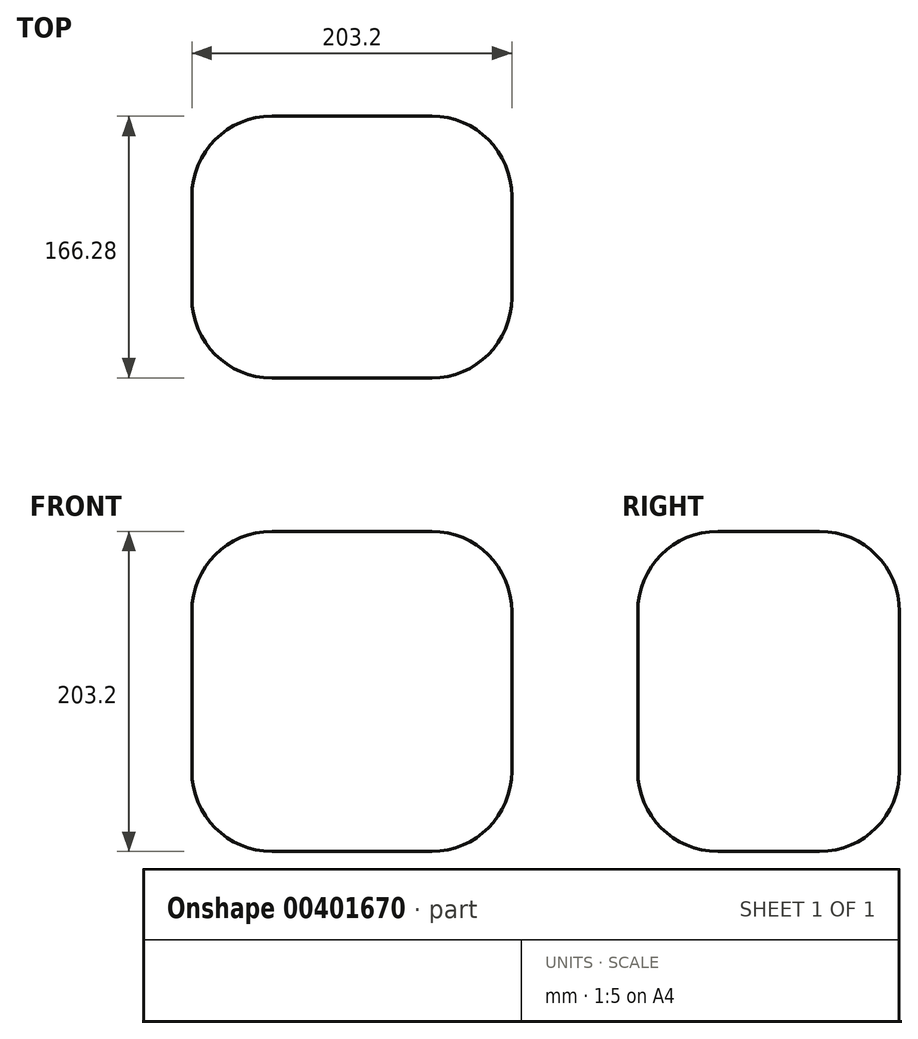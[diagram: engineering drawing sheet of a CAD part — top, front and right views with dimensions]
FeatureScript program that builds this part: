
annotation { "Feature Type Name" : "Feature", "Feature Type Description" : "" }
export const myFeature = defineFeature(function(context is Context, id is Id, definition is map)
    precondition{}
    {
        {
            var Q0;
            Q0=qCreatedBy(makeId("Front.planeOp"),FACE);
            var sketch = newSketch(context, id + "F0", { "sketchPlane" : qUnion([Q0])});
            skLineSegment(sketch, "E0.bottom", {"start": v(-100.4, 111.28) * mm, "end": v(102.8, 111.28) * mm});
            skLineSegment(sketch, "E0.top", {"start": v(-100.4, -91.92) * mm, "end": v(102.8, -91.92) * mm});
            skLineSegment(sketch, "E0.left", {"start": v(-100.4, 111.28) * mm, "end": v(-100.4, -91.92) * mm});
            skLineSegment(sketch, "E0.right", {"start": v(102.8, 111.28) * mm, "end": v(102.8, -91.92) * mm});
            skSolve(sketch);
        }
        {
            var Q0;
            Q0 = qSketchRegion(id + "F0", true);
            extrude(context, id + "F1", {"entities" : qUnion([Q0]), "depth" : 166.28 * mm});
        }
        {
            var Q0;
            Q0=makeQuery(id+"F1.opExtrude","SWEPT_EDGE",EDGE,{"disambiguationData":[OSD([sQuery(id+"F0.wireOp",EDGE,"E0.bottom"),sQuery(id+"F0.wireOp",EDGE,"E0.right")])]});
            var Q1;
            Q1=makeQuery(id+"F1.opExtrude","CAP_EDGE",EDGE,{"disambiguationData":[OSD([sQuery(id+"F0.wireOp",EDGE,"E0.bottom")])],"isStart":false});
            var Q2;
            Q2=makeQuery(id+"F1.opExtrude","CAP_EDGE",EDGE,{"disambiguationData":[OSD([sQuery(id+"F0.wireOp",EDGE,"E0.right")])],"isStart":false});
            var Q3;
            Q3=makeQuery(id+"F1.opExtrude","CAP_EDGE",EDGE,{"disambiguationData":[OSD([sQuery(id+"F0.wireOp",EDGE,"E0.bottom")])],"isStart":true});
            var Q4;
            Q4=makeQuery(id+"F1.opExtrude","SWEPT_EDGE",EDGE,{"disambiguationData":[OSD([sQuery(id+"F0.wireOp",EDGE,"E0.bottom"),sQuery(id+"F0.wireOp",EDGE,"E0.left")])]});
            var Q5;
            Q5=makeQuery(id+"F1.opExtrude","CAP_EDGE",EDGE,{"disambiguationData":[OSD([sQuery(id+"F0.wireOp",EDGE,"E0.left")])],"isStart":false});
            var Q6;
            Q6=makeQuery(id+"F1.opExtrude","CAP_EDGE",EDGE,{"disambiguationData":[OSD([sQuery(id+"F0.wireOp",EDGE,"E0.top")])],"isStart":false});
            var Q7;
            Q7=makeQuery(id+"F1.opExtrude","SWEPT_EDGE",EDGE,{"disambiguationData":[OSD([sQuery(id+"F0.wireOp",EDGE,"E0.top"),sQuery(id+"F0.wireOp",EDGE,"E0.right")])]});
            var Q8;
            Q8=makeQuery(id+"F1.opExtrude","CAP_EDGE",EDGE,{"disambiguationData":[OSD([sQuery(id+"F0.wireOp",EDGE,"E0.right")])],"isStart":true});
            var Q9;
            Q9=makeQuery(id+"F1.opExtrude","CAP_EDGE",EDGE,{"disambiguationData":[OSD([sQuery(id+"F0.wireOp",EDGE,"E0.top")])],"isStart":true});
            var Q10;
            Q10=makeQuery(id+"F1.opExtrude","SWEPT_EDGE",EDGE,{"disambiguationData":[OSD([sQuery(id+"F0.wireOp",EDGE,"E0.top"),sQuery(id+"F0.wireOp",EDGE,"E0.left")])]});
            var Q11;
            Q11=makeQuery(id+"F1.opExtrude","CAP_EDGE",EDGE,{"disambiguationData":[OSD([sQuery(id+"F0.wireOp",EDGE,"E0.left")])],"isStart":true});
            fillet(context, id + "F2", {"entities" : qUnion([Q0, Q1, Q2, Q3, Q4, Q5, Q6, Q7, Q8, Q9, Q10, Q11]), "radius" : 50.8 * mm, "tangentPropagation" : true, "allowEdgeOverflow" : false});
        }
    });
